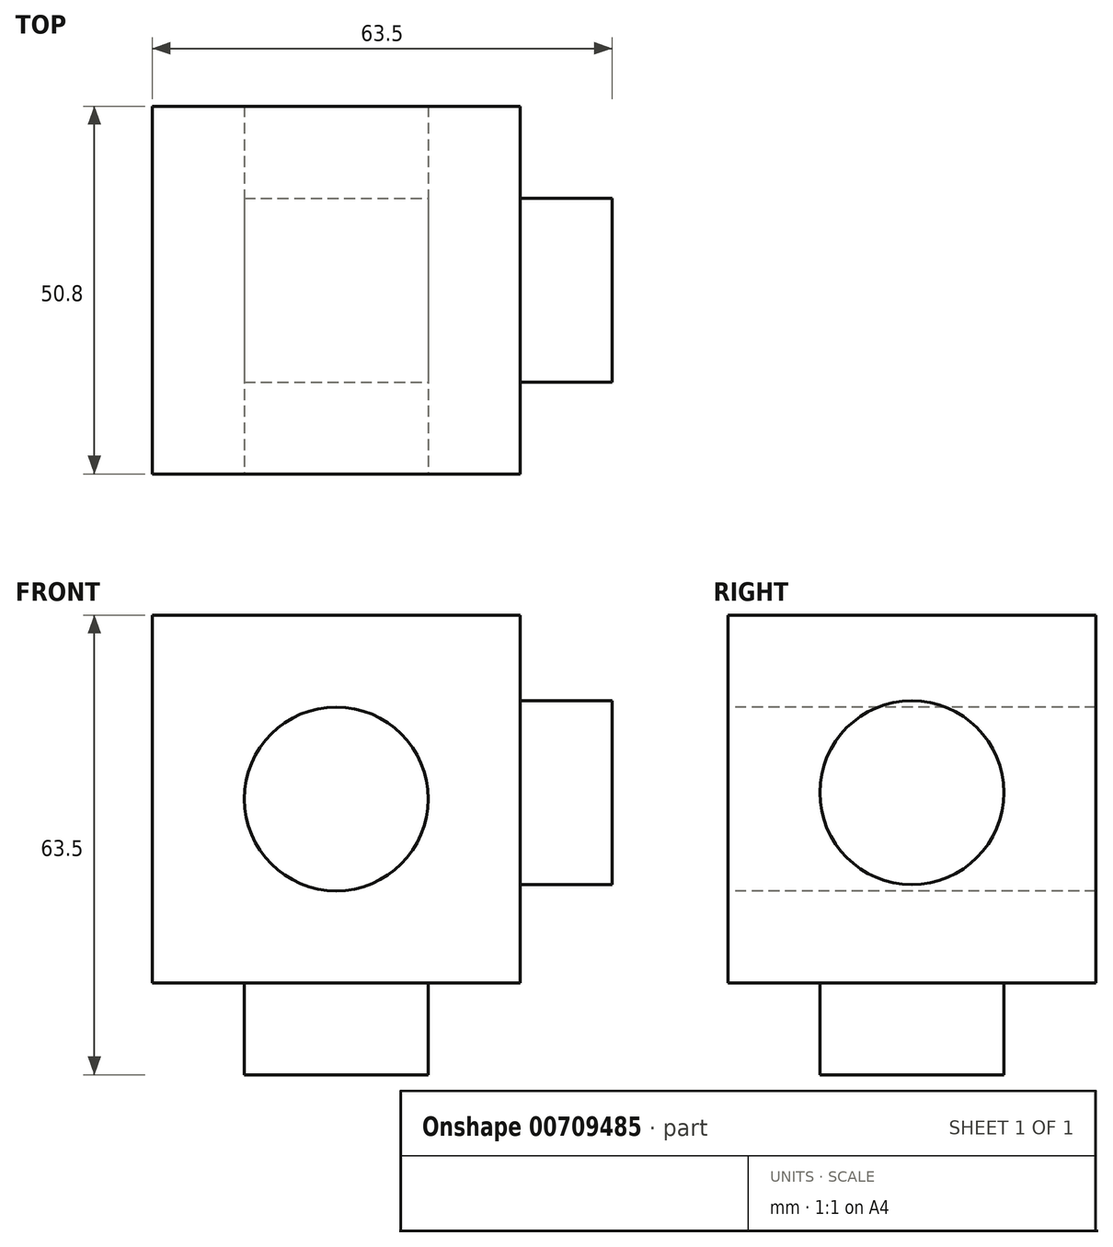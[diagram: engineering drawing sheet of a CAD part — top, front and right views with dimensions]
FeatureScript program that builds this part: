
annotation { "Feature Type Name" : "Feature", "Feature Type Description" : "" }
export const myFeature = defineFeature(function(context is Context, id is Id, definition is map)
    precondition{}
    {
        {
            var Q0;
            Q0=qCreatedBy(makeId("Front.planeOp"),FACE);
            var sketch = newSketch(context, id + "F0", { "sketchPlane" : qUnion([Q0])});
            skLineSegment(sketch, "E0.bottom", {"start": v(0, 0) * mm, "end": v(-50.8, 0) * mm});
            skLineSegment(sketch, "E0.top", {"start": v(0, 50.8) * mm, "end": v(-50.8, 50.8) * mm});
            skLineSegment(sketch, "E0.left", {"start": v(0, 0) * mm, "end": v(0, 50.8) * mm});
            skLineSegment(sketch, "E0.right", {"start": v(-50.8, 0) * mm, "end": v(-50.8, 50.8) * mm});
            skSolve(sketch);
        }
        {
            var Q0;
            Q0 = qSketchRegion(id + "F0", true);
            extrude(context, id + "F1", {"entities" : qUnion([Q0]), "depth" : 50.8 * mm, "offsetDistance" : 25.4 * mm});
        }
        {
            var Q0;
            Q0=makeQuery(id+"F1.opExtrude","CAP_FACE",FACE,{"disambiguationData":[OSD([sQuery(id+"F0.wireOp",EDGE,"E0.bottom"),sQuery(id+"F0.wireOp",EDGE,"E0.top"),sQuery(id+"F0.wireOp",EDGE,"E0.left"),sQuery(id+"F0.wireOp",EDGE,"E0.right")])],"isStart":false});
            var sketch = newSketch(context, id + "F2", { "sketchPlane" : qUnion([Q0])});
            skCircle(sketch, "E1", {"center": v(-25.4, 25.4) * mm, "radius": 12.7 * mm});
            skSolve(sketch);
        }
        {
            var Q0;
            Q0 = qSketchRegion(id + "F2", true);
            extrude(context, id + "F3", {"entities" : qUnion([Q0]), "operationType" : NewBodyOperationType.REMOVE, "oppositeDirection" : true, "depth" : 50.8 * mm, "offsetDistance" : 25.4 * mm});
        }
        {
            var Q0;
            Q0=qCreatedBy(makeId("Right.planeOp"),FACE);
            var sketch = newSketch(context, id + "F4", { "sketchPlane" : qUnion([Q0])});
            skCircle(sketch, "E2", {"center": v(-25.41, 26.27) * mm, "radius": 12.7 * mm});
            skSolve(sketch);
        }
        {
            var Q0;
            Q0=makeQuery(id+"F4.imprint","IMPRINT",FACE,{"disambiguationData":[TD([[makeQuery(id+"F4.imprint","IMPRINT",EDGE,{"derivedFrom":sQuery(id+"F4.wireOp",EDGE,"E2")}),1.0]])]});
            extrude(context, id + "F5", {"entities" : qUnion([Q0]), "operationType" : NewBodyOperationType.ADD, "depth" : 12.7 * mm, "offsetDistance" : 25.4 * mm});
        }
        {
            var Q0;
            Q0=makeQuery(id+"F1.opExtrude","SWEPT_FACE",FACE,{"disambiguationData":[OSD([sQuery(id+"F0.wireOp",EDGE,"E0.bottom")])]});
            var sketch = newSketch(context, id + "F6", { "sketchPlane" : qUnion([Q0])});
            skSolve(sketch);
        }
        {
            var Q0;
            {var subQ0=sQuery(id+"F0.wireOp",EDGE,"E0.bottom");Q0=makeQuery(id+"F6.imprint","IMPRINT",FACE,{"disambiguationData":[TD([[makeQuery(id+"F6.imprint","IMPRINT",EDGE,{"derivedFrom":makeQuery(id+"F1.opExtrude","CAP_EDGE",EDGE,{"disambiguationData":[OSD([subQ0])],"isStart":true})}),-1.0]])]});}
            var sketch = newSketch(context, id + "F7", { "sketchPlane" : qUnion([Q0])});
            skLineSegment(sketch, "E3.bottom", {"start": v(-38.1, 12.7) * mm, "end": v(-12.7, 12.7) * mm});
            skLineSegment(sketch, "E3.top", {"start": v(-38.1, 38.1) * mm, "end": v(-12.7, 38.1) * mm});
            skLineSegment(sketch, "E3.left", {"start": v(-38.1, 12.7) * mm, "end": v(-38.1, 38.1) * mm});
            skLineSegment(sketch, "E3.right", {"start": v(-12.7, 12.7) * mm, "end": v(-12.7, 38.1) * mm});
            skSolve(sketch);
        }
        {
            var Q0;
            Q0 = qSketchRegion(id + "F7", true);
            extrude(context, id + "F8", {"entities" : qUnion([Q0]), "operationType" : NewBodyOperationType.ADD, "depth" : 12.7 * mm, "offsetDistance" : 25.4 * mm});
        }
    });
